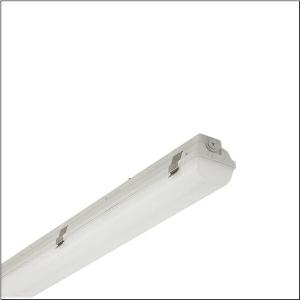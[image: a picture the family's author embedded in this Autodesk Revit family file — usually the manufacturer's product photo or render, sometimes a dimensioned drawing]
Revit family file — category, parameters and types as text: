
# Revit family: monsun_r__21_eco_51fj20mp47a_a802
name_source: partatom
category: Lighting Fixtures
units: mm (PartAtom-declared; Revit-internal decimal feet)

## family parameters
Cut with Voids When Loaded = No
Host = Face
Light Source = No
Part Type = Normal
Room Calculation Point = No
Round Connector Dimension = Use Diameter
Shared = No

## types (1)
- --- (1 x LED, 6600 lm, 50 W, 4000K)
    Apparent Load = 50 VA
    CIE Flux Codes = 40 69 88 88 100
    Color Rendering = 80
    Color Temperature = 4000K
    Default Elevation = 1800 mm
    Description = Monsun® 21 Eco, damp-proof luminaire, primary optical cover: diffuser, of PC, UV-stabilised, frosted, light emission: direct distribution, primary light characteristic: symmetric, installation type: suspended mounting, surface-mounted, LED, rated luminous flux: 6.600lm, luminous efficacy: 132lm/W, light colour: 840, colour temperature: 4000K, control gear: ECG Multilumen, with terminal, 3-pole, max. 2.5mm², mains connection: 220..240V, AC, 50/60Hz, rated input power: 50W, housing, of glass-fibre reinforced polyester, light grey (RAL 7035), length: 1.577mm, width: 90mm, height: 95mm, clip for enclosure, of spring steel V2A, protection rating (complete): IP66, insulation class (complete): insulation class I (protective earthing), certification: CE, UKCA, protection symbol: D, impact resistance: IK08, permissible operating ambient temperature: -20..+35°C, corresponds to IFS (International Featured Standards) requirements for safety and quality in the food industry, contact your sales advisor before using the luminaires in applications with unclear chemical exposure, large temperature fluctuations or condensation-forming humidity, packaging unit: 1 piece
    Height = 103 mm
    Lamp = 1 x LED
    Lamp Light Flux = 6600 lm
    Lamp Power = 50 W
    Lamp count = 1
    Length = 1577 mm
    Luminous efficacy = 132 lm/W
    Manufacturer = Siteco
    ModVariant = No
    Model = 51FJ20MP47A
    Mounting Place = Ceiling
    Mounting Type = Surface mounted
    Number of Poles = 1
    OnlyDefault = Yes
    Power Factor = 1
    Product Name = Monsun® 21 Eco
    Product group = damp-proof luminaire
    ProductGroupID = 301
    Protection Class = Protection class I
    Protection Degree = IP 66
    RLX_Detail_Level = 1
    RLX_Emergency_Light_Flux = 0 lm
    RLX_Emergency_Type = 0
    RLX_Emergency_Type_DB = No
    RlxData = <blob elided: 34109 chars, md5=74ebba2c>
    Socket = socket
    Standby Power = 0 W
    System Light Flux = 6600 lm
    System Power = 50 W
    Type Comments = factory setting: luminous flux: 100 % | (ON | ON) | 350 mA
    Type Image = l_1007218.jpg
    URL = http://relux.com
    VarID = @adj_095745
    Voltage = 0 V
    Weight = 0.00 kg
    Width = 90 mm

## geometry (parser evidence)
native form markers: Blend x4, Sweep x12
no freeform markers — native parametric forms only
